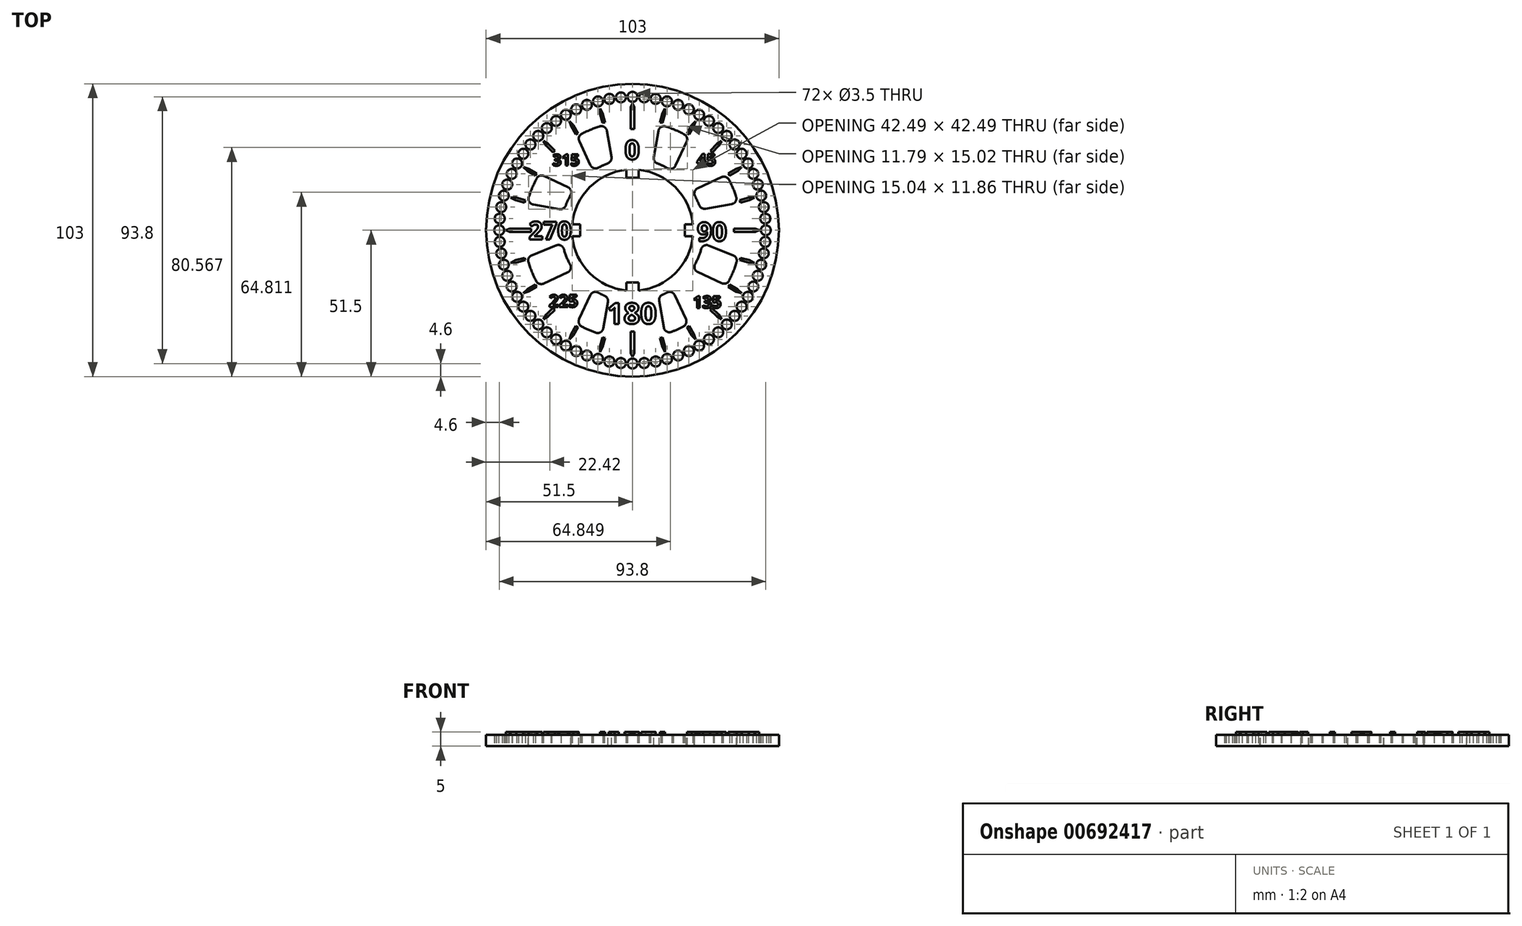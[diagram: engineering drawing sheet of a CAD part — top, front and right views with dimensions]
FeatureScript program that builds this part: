
annotation { "Feature Type Name" : "Feature", "Feature Type Description" : "" }
export const myFeature = defineFeature(function(context is Context, id is Id, definition is map)
    precondition{}
    {
        {
            var Q0;
            Q0=qCreatedBy(makeId("Top.planeOp"),FACE);
            var sketch = newSketch(context, id + "F0", { "sketchPlane" : qUnion([Q0])});
            skArc(sketch, "E0", {"start": v(-2.45, 20.86) * mm, "mid": v(-14.85, 14.85) * mm, "end": v(-20.86, 2.45) * mm});
            skLineSegment(sketch, "E1", {"start": v(0, 35.66) * mm, "end": v(0, -32.33) * mm, "construction": true});
            skLineSegment(sketch, "E2", {"start": v(-36.79, 0) * mm, "end": v(39.43, 0) * mm, "construction": true});
            skCircle(sketch, "E3", {"center": v(0, 0) * mm, "radius": 21.35 * mm});
            skLineSegment(sketch, "E4", {"start": v(0, 18.06) * mm, "end": v(-2.45, 18.06) * mm});
            skLineSegment(sketch, "E5", {"start": v(-2.45, 18.06) * mm, "end": v(-2.45, 20.86) * mm});
            skLineSegment(sketch, "E6.MirrorCS", {"start": v(0, 18.06) * mm, "end": v(2.45, 18.06) * mm});
            skLineSegment(sketch, "E7.MirrorCS", {"start": v(2.45, 18.06) * mm, "end": v(2.45, 20.86) * mm});
            skLineSegment(sketch, "E8.1.0", {"start": v(-18.06, -2.45) * mm, "end": v(-20.86, -2.45) * mm});
            skLineSegment(sketch, "E8.1.1", {"start": v(-18.06, 0) * mm, "end": v(-18.06, -2.45) * mm});
            skLineSegment(sketch, "E8.1.2", {"start": v(-18.06, 0) * mm, "end": v(-18.06, 2.45) * mm});
            skLineSegment(sketch, "E8.1.3", {"start": v(-18.06, 2.45) * mm, "end": v(-20.86, 2.45) * mm});
            skLineSegment(sketch, "E8.2.0", {"start": v(2.45, -18.06) * mm, "end": v(2.45, -20.86) * mm});
            skLineSegment(sketch, "E8.2.1", {"start": v(0, -18.06) * mm, "end": v(2.45, -18.06) * mm});
            skLineSegment(sketch, "E8.2.2", {"start": v(0, -18.06) * mm, "end": v(-2.45, -18.06) * mm});
            skLineSegment(sketch, "E8.2.3", {"start": v(-2.45, -18.06) * mm, "end": v(-2.45, -20.86) * mm});
            skLineSegment(sketch, "E8.3.0", {"start": v(18.06, 2.45) * mm, "end": v(20.86, 2.45) * mm});
            skLineSegment(sketch, "E8.3.1", {"start": v(18.06, 0) * mm, "end": v(18.06, 2.45) * mm});
            skLineSegment(sketch, "E8.3.2", {"start": v(18.06, 0) * mm, "end": v(18.06, -2.45) * mm});
            skLineSegment(sketch, "E8.3.3", {"start": v(18.06, -2.45) * mm, "end": v(20.86, -2.45) * mm});
            skArc(sketch, "E9.trimOffspring", {"start": v(20.86, 2.45) * mm, "mid": v(14.85, 14.85) * mm, "end": v(2.45, 20.86) * mm});
            skArc(sketch, "E10.trimOffspring", {"start": v(2.45, -20.86) * mm, "mid": v(14.85, -14.85) * mm, "end": v(20.86, -2.45) * mm});
            skArc(sketch, "E11.trimOffspring", {"start": v(-20.86, -2.45) * mm, "mid": v(-14.85, -14.85) * mm, "end": v(-2.45, -20.86) * mm});
            skCircle(sketch, "E12", {"center": v(0, 0) * mm, "radius": 24.63 * mm});
            skLineSegment(sketch, "E13", {"start": v(-1.6, 24.58) * mm, "end": v(-1.6, 48.9) * mm});
            skLineSegment(sketch, "E14", {"start": v(-1.6, 48.9) * mm, "end": v(1.67, 48.9) * mm});
            skLineSegment(sketch, "E15", {"start": v(1.67, 48.9) * mm, "end": v(1.67, 24.58) * mm});
            skCircle(sketch, "E16", {"center": v(0, 0) * mm, "radius": 21 * mm, "construction": true});
            skPoint(sketch, "E17", {"position": v(0, 21) * mm});
            skLineSegment(sketch, "E18", {"start": v(-7.13, 21) * mm, "end": v(7.07, 21) * mm, "construction": true});
            skPoint(sketch, "E19", {"position": v(0, 46.9) * mm});
            skLineSegment(sketch, "E20", {"start": v(-18.06, 46.9) * mm, "end": v(18.78, 46.9) * mm, "construction": true});
            skCircle(sketch, "E21", {"center": v(0, 46.9) * mm, "radius": 1.75 * mm});
            skLineSegment(sketch, "E22", {"start": v(-2.1, 21.25) * mm, "end": v(-2.1, 18.4) * mm});
            skLineSegment(sketch, "E23", {"start": v(-2.1, 18.4) * mm, "end": v(2.1, 18.4) * mm});
            skLineSegment(sketch, "E24", {"start": v(2.1, 18.4) * mm, "end": v(2.1, 21.25) * mm});
            skLineSegment(sketch, "E25.1.0", {"start": v(-21.25, -2.1) * mm, "end": v(-18.4, -2.1) * mm});
            skLineSegment(sketch, "E25.1.1", {"start": v(-18.4, -2.1) * mm, "end": v(-18.4, 2.1) * mm});
            skLineSegment(sketch, "E25.1.2", {"start": v(-18.4, 2.1) * mm, "end": v(-21.25, 2.1) * mm});
            skLineSegment(sketch, "E25.2.0", {"start": v(2.1, -21.25) * mm, "end": v(2.1, -18.4) * mm});
            skLineSegment(sketch, "E25.2.1", {"start": v(2.1, -18.4) * mm, "end": v(-2.1, -18.4) * mm});
            skLineSegment(sketch, "E25.2.2", {"start": v(-2.1, -18.4) * mm, "end": v(-2.1, -21.25) * mm});
            skLineSegment(sketch, "E25.3.0", {"start": v(21.25, 2.1) * mm, "end": v(18.4, 2.1) * mm});
            skLineSegment(sketch, "E25.3.1", {"start": v(18.4, 2.1) * mm, "end": v(18.4, -2.1) * mm});
            skLineSegment(sketch, "E25.3.2", {"start": v(18.4, -2.1) * mm, "end": v(21.25, -2.1) * mm});
            skCircle(sketch, "E26", {"center": v(0, 46.9) * mm, "radius": 4.35 * mm});
            skCircle(sketch, "E27", {"center": v(0, 0) * mm, "radius": 51.5 * mm});
            skCircle(sketch, "E28.1.0", {"center": v(-4.09, 46.72) * mm, "radius": 1.75 * mm});
            skCircle(sketch, "E28.2.0", {"center": v(-8.14, 46.19) * mm, "radius": 1.75 * mm});
            skCircle(sketch, "E28.3.0", {"center": v(-12.14, 45.3) * mm, "radius": 1.75 * mm});
            skCircle(sketch, "E28.4.0", {"center": v(-16.04, 44.07) * mm, "radius": 1.75 * mm});
            skCircle(sketch, "E28.5.0", {"center": v(-19.82, 42.5) * mm, "radius": 1.75 * mm});
            skCircle(sketch, "E28.6.0", {"center": v(-23.45, 40.62) * mm, "radius": 1.75 * mm});
            skCircle(sketch, "E28.7.0", {"center": v(-26.9, 38.42) * mm, "radius": 1.75 * mm});
            skCircle(sketch, "E28.8.0", {"center": v(-30.15, 35.93) * mm, "radius": 1.75 * mm});
            skCircle(sketch, "E28.9.0", {"center": v(-33.16, 33.16) * mm, "radius": 1.75 * mm});
            skCircle(sketch, "E28.10.0", {"center": v(-35.93, 30.15) * mm, "radius": 1.75 * mm});
            skCircle(sketch, "E28.11.0", {"center": v(-38.42, 26.9) * mm, "radius": 1.75 * mm});
            skCircle(sketch, "E28.12.0", {"center": v(-40.62, 23.45) * mm, "radius": 1.75 * mm});
            skCircle(sketch, "E28.13.0", {"center": v(-42.5, 19.82) * mm, "radius": 1.75 * mm});
            skCircle(sketch, "E28.14.0", {"center": v(-44.07, 16.04) * mm, "radius": 1.75 * mm});
            skCircle(sketch, "E28.15.0", {"center": v(-45.3, 12.14) * mm, "radius": 1.75 * mm});
            skCircle(sketch, "E28.16.0", {"center": v(-46.19, 8.14) * mm, "radius": 1.75 * mm});
            skCircle(sketch, "E28.17.0", {"center": v(-46.72, 4.09) * mm, "radius": 1.75 * mm});
            skCircle(sketch, "E28.18.0", {"center": v(-46.9, 0) * mm, "radius": 1.75 * mm});
            skCircle(sketch, "E28.19.0", {"center": v(-46.72, -4.09) * mm, "radius": 1.75 * mm});
            skCircle(sketch, "E28.20.0", {"center": v(-46.19, -8.14) * mm, "radius": 1.75 * mm});
            skCircle(sketch, "E28.21.0", {"center": v(-45.3, -12.14) * mm, "radius": 1.75 * mm});
            skCircle(sketch, "E28.22.0", {"center": v(-44.07, -16.04) * mm, "radius": 1.75 * mm});
            skCircle(sketch, "E28.23.0", {"center": v(-42.5, -19.82) * mm, "radius": 1.75 * mm});
            skCircle(sketch, "E28.24.0", {"center": v(-40.62, -23.45) * mm, "radius": 1.75 * mm});
            skCircle(sketch, "E28.25.0", {"center": v(-38.42, -26.9) * mm, "radius": 1.75 * mm});
            skCircle(sketch, "E28.26.0", {"center": v(-35.93, -30.15) * mm, "radius": 1.75 * mm});
            skCircle(sketch, "E28.27.0", {"center": v(-33.16, -33.16) * mm, "radius": 1.75 * mm});
            skCircle(sketch, "E28.28.0", {"center": v(-30.15, -35.93) * mm, "radius": 1.75 * mm});
            skCircle(sketch, "E28.29.0", {"center": v(-26.9, -38.42) * mm, "radius": 1.75 * mm});
            skCircle(sketch, "E28.30.0", {"center": v(-23.45, -40.62) * mm, "radius": 1.75 * mm});
            skCircle(sketch, "E28.31.0", {"center": v(-19.82, -42.5) * mm, "radius": 1.75 * mm});
            skCircle(sketch, "E28.32.0", {"center": v(-16.04, -44.07) * mm, "radius": 1.75 * mm});
            skCircle(sketch, "E28.33.0", {"center": v(-12.14, -45.3) * mm, "radius": 1.75 * mm});
            skCircle(sketch, "E28.34.0", {"center": v(-8.14, -46.19) * mm, "radius": 1.75 * mm});
            skCircle(sketch, "E28.35.0", {"center": v(-4.09, -46.72) * mm, "radius": 1.75 * mm});
            skCircle(sketch, "E28.36.0", {"center": v(0, -46.9) * mm, "radius": 1.75 * mm});
            skCircle(sketch, "E28.37.0", {"center": v(4.09, -46.72) * mm, "radius": 1.75 * mm});
            skCircle(sketch, "E28.38.0", {"center": v(8.14, -46.19) * mm, "radius": 1.75 * mm});
            skCircle(sketch, "E28.39.0", {"center": v(12.14, -45.3) * mm, "radius": 1.75 * mm});
            skCircle(sketch, "E28.40.0", {"center": v(16.04, -44.07) * mm, "radius": 1.75 * mm});
            skCircle(sketch, "E28.41.0", {"center": v(19.82, -42.5) * mm, "radius": 1.75 * mm});
            skCircle(sketch, "E28.42.0", {"center": v(23.45, -40.62) * mm, "radius": 1.75 * mm});
            skCircle(sketch, "E28.43.0", {"center": v(26.9, -38.42) * mm, "radius": 1.75 * mm});
            skCircle(sketch, "E28.44.0", {"center": v(30.15, -35.93) * mm, "radius": 1.75 * mm});
            skCircle(sketch, "E28.45.0", {"center": v(33.16, -33.16) * mm, "radius": 1.75 * mm});
            skCircle(sketch, "E28.46.0", {"center": v(35.93, -30.15) * mm, "radius": 1.75 * mm});
            skCircle(sketch, "E28.47.0", {"center": v(38.42, -26.9) * mm, "radius": 1.75 * mm});
            skCircle(sketch, "E28.48.0", {"center": v(40.62, -23.45) * mm, "radius": 1.75 * mm});
            skCircle(sketch, "E28.49.0", {"center": v(42.5, -19.82) * mm, "radius": 1.75 * mm});
            skCircle(sketch, "E28.50.0", {"center": v(44.07, -16.04) * mm, "radius": 1.75 * mm});
            skCircle(sketch, "E28.51.0", {"center": v(45.3, -12.14) * mm, "radius": 1.75 * mm});
            skCircle(sketch, "E28.52.0", {"center": v(46.19, -8.14) * mm, "radius": 1.75 * mm});
            skCircle(sketch, "E28.53.0", {"center": v(46.72, -4.09) * mm, "radius": 1.75 * mm});
            skCircle(sketch, "E28.54.0", {"center": v(46.9, 0) * mm, "radius": 1.75 * mm});
            skCircle(sketch, "E28.55.0", {"center": v(46.72, 4.09) * mm, "radius": 1.75 * mm});
            skCircle(sketch, "E28.56.0", {"center": v(46.19, 8.14) * mm, "radius": 1.75 * mm});
            skCircle(sketch, "E28.57.0", {"center": v(45.3, 12.14) * mm, "radius": 1.75 * mm});
            skCircle(sketch, "E28.58.0", {"center": v(44.07, 16.04) * mm, "radius": 1.75 * mm});
            skCircle(sketch, "E28.59.0", {"center": v(42.5, 19.82) * mm, "radius": 1.75 * mm});
            skCircle(sketch, "E28.60.0", {"center": v(40.62, 23.45) * mm, "radius": 1.75 * mm});
            skCircle(sketch, "E28.61.0", {"center": v(38.42, 26.9) * mm, "radius": 1.75 * mm});
            skCircle(sketch, "E28.62.0", {"center": v(35.93, 30.15) * mm, "radius": 1.75 * mm});
            skCircle(sketch, "E28.63.0", {"center": v(33.16, 33.16) * mm, "radius": 1.75 * mm});
            skCircle(sketch, "E28.64.0", {"center": v(30.15, 35.93) * mm, "radius": 1.75 * mm});
            skCircle(sketch, "E28.65.0", {"center": v(26.9, 38.42) * mm, "radius": 1.75 * mm});
            skCircle(sketch, "E28.66.0", {"center": v(23.45, 40.62) * mm, "radius": 1.75 * mm});
            skCircle(sketch, "E28.67.0", {"center": v(19.82, 42.5) * mm, "radius": 1.75 * mm});
            skCircle(sketch, "E28.68.0", {"center": v(16.04, 44.07) * mm, "radius": 1.75 * mm});
            skCircle(sketch, "E28.69.0", {"center": v(12.14, 45.3) * mm, "radius": 1.75 * mm});
            skCircle(sketch, "E28.70.0", {"center": v(8.14, 46.19) * mm, "radius": 1.75 * mm});
            skCircle(sketch, "E28.71.0", {"center": v(4.09, 46.72) * mm, "radius": 1.75 * mm});
            skCircle(sketch, "E29", {"center": v(0, 0) * mm, "radius": 42.33 * mm});
            skCircle(sketch, "E30", {"center": v(0, 0) * mm, "radius": 27.68 * mm});
            skSolve(sketch);
        }
        {
            var Q0;
            Q0=makeQuery(id+"F0.imprint","IMPRINT",FACE,{"disambiguationData":[TD([[makeQuery(id+"F0.imprint","IMPRINT",EDGE,{"derivedFrom":sQuery(id+"F0.wireOp",EDGE,"E27")}),1.0]])]});
            var Q1;
            {var subQ16=sQuery(id+"F0.wireOp",EDGE,"E14");Q1=makeQuery(id+"F0.imprint","IMPRINT",FACE,{"disambiguationData":[TD([[makeQuery(id+"F0.imprint","IMPRINT",EDGE,{"derivedFrom":subQ16}),1.0]])]});}
            var Q2;
            {var subQ0=sQuery(id+"F0.wireOp",EDGE,"E26");var subQ1=sQuery(id+"F0.wireOp",EDGE,"E13");var subQ2=makeQuery(id+"F0.imprint","INTERSECT",VERTEX,{"derivedFrom":[subQ1,subQ0]});Q2=makeQuery(id+"F0.imprint","IMPRINT",FACE,{"disambiguationData":[TD([[makeQuery(id+"F0.imprint","IMPRINT",EDGE,{"disambiguationData":[TD([[subQ2,-1.0]])],"derivedFrom":subQ1}),-1.0]])]});}
            var Q3;
            {var subQ0=sQuery(id+"F0.wireOp",EDGE,"E14");Q3=makeQuery(id+"F0.imprint","IMPRINT",FACE,{"disambiguationData":[TD([[makeQuery(id+"F0.imprint","IMPRINT",EDGE,{"derivedFrom":subQ0}),-1.0]])]});}
            var Q4;
            {var subQ0=sQuery(id+"F0.wireOp",EDGE,"E13");var subQ1=sQuery(id+"F0.wireOp",EDGE,"E12");var subQ2=makeQuery(id+"F0.imprint","INTERSECT",VERTEX,{"derivedFrom":[subQ1,subQ0]});Q4=makeQuery(id+"F0.imprint","IMPRINT",FACE,{"disambiguationData":[TD([[makeQuery(id+"F0.imprint","IMPRINT",EDGE,{"disambiguationData":[TD([[subQ2,1.0]])],"derivedFrom":subQ1}),-1.0]])]});}
            var Q5;
            {var subQ0=sQuery(id+"F0.wireOp",EDGE,"E3");var subQ4=makeQuery(id+"F0.imprint","INTERSECT",VERTEX,{"derivedFrom":[subQ0,sQuery(id+"F0.wireOp",EDGE,"E24")]});Q5=makeQuery(id+"F0.imprint","IMPRINT",FACE,{"disambiguationData":[TD([[makeQuery(id+"F0.imprint","IMPRINT",EDGE,{"disambiguationData":[TD([[subQ4,1.0]])],"derivedFrom":subQ0}),-1.0]])]});}
            var Q6;
            {var subQ5=sQuery(id+"F0.wireOp",EDGE,"E25.1.1");Q6=makeQuery(id+"F0.imprint","IMPRINT",FACE,{"disambiguationData":[TD([[makeQuery(id+"F0.imprint","IMPRINT",EDGE,{"derivedFrom":subQ5}),1.0]])]});}
            var Q7;
            {var subQ0=sQuery(id+"F0.wireOp",EDGE,"E22");Q7=makeQuery(id+"F0.imprint","IMPRINT",FACE,{"disambiguationData":[TD([[makeQuery(id+"F0.imprint","IMPRINT",EDGE,{"derivedFrom":subQ0}),1.0]])]});}
            var Q8;
            {var subQ5=sQuery(id+"F0.wireOp",EDGE,"E25.3.1");Q8=makeQuery(id+"F0.imprint","IMPRINT",FACE,{"disambiguationData":[TD([[makeQuery(id+"F0.imprint","IMPRINT",EDGE,{"derivedFrom":subQ5}),1.0]])]});}
            var Q9;
            {var subQ5=sQuery(id+"F0.wireOp",EDGE,"E25.2.1");Q9=makeQuery(id+"F0.imprint","IMPRINT",FACE,{"disambiguationData":[TD([[makeQuery(id+"F0.imprint","IMPRINT",EDGE,{"derivedFrom":subQ5}),1.0]])]});}
            var Q10;
            {var subQ0=sQuery(id+"F0.wireOp",EDGE,"E30");var subQ1=sQuery(id+"F0.wireOp",EDGE,"E13");var subQ2=makeQuery(id+"F0.imprint","INTERSECT",VERTEX,{"derivedFrom":[subQ1,subQ0]});Q10=makeQuery(id+"F0.imprint","IMPRINT",FACE,{"disambiguationData":[TD([[makeQuery(id+"F0.imprint","IMPRINT",EDGE,{"disambiguationData":[TD([[subQ2,-1.0]])],"derivedFrom":subQ1}),1.0]])]});}
            var Q11;
            {var subQ0=sQuery(id+"F0.wireOp",EDGE,"E13");var subQ1=sQuery(id+"F0.wireOp",EDGE,"E12");var subQ2=makeQuery(id+"F0.imprint","INTERSECT",VERTEX,{"derivedFrom":[subQ1,subQ0]});Q11=makeQuery(id+"F0.imprint","IMPRINT",FACE,{"disambiguationData":[TD([[makeQuery(id+"F0.imprint","IMPRINT",EDGE,{"disambiguationData":[TD([[subQ2,-1.0]])],"derivedFrom":subQ1}),-1.0]])]});}
            var Q12;
            {var subQ0=sQuery(id+"F0.wireOp",EDGE,"E30");var subQ1=sQuery(id+"F0.wireOp",EDGE,"E13");var subQ2=makeQuery(id+"F0.imprint","INTERSECT",VERTEX,{"derivedFrom":[subQ1,subQ0]});Q12=makeQuery(id+"F0.imprint","IMPRINT",FACE,{"disambiguationData":[TD([[makeQuery(id+"F0.imprint","IMPRINT",EDGE,{"disambiguationData":[TD([[subQ2,-1.0]])],"derivedFrom":subQ1}),-1.0]])]});}
            var Q13;
            {var subQ0=sQuery(id+"F0.wireOp",EDGE,"E29");var subQ1=sQuery(id+"F0.wireOp",EDGE,"E13");var subQ2=makeQuery(id+"F0.imprint","INTERSECT",VERTEX,{"derivedFrom":[subQ1,subQ0]});Q13=makeQuery(id+"F0.imprint","IMPRINT",FACE,{"disambiguationData":[TD([[makeQuery(id+"F0.imprint","IMPRINT",EDGE,{"disambiguationData":[TD([[subQ2,-1.0]])],"derivedFrom":subQ1}),-1.0]])]});}
            extrude(context, id + "F1", {"entities" : qUnion([Q0, Q1, Q2, Q3, Q4, Q5, Q6, Q7, Q8, Q9, Q10, Q11, Q12, Q13]), "depth" : 4 * mm});
        }
        {
            var Q0;
            Q0=makeQuery(id+"F1.opExtrude","CAP_FACE",FACE,{"disambiguationData":[OSD([sQuery(id+"F0.wireOp",EDGE,"E3"),sQuery(id+"F0.wireOp",EDGE,"E21"),sQuery(id+"F0.wireOp",EDGE,"E22"),sQuery(id+"F0.wireOp",EDGE,"E23"),sQuery(id+"F0.wireOp",EDGE,"E24"),sQuery(id+"F0.wireOp",EDGE,"E25.1.0"),sQuery(id+"F0.wireOp",EDGE,"E25.1.1"),sQuery(id+"F0.wireOp",EDGE,"E25.1.2"),sQuery(id+"F0.wireOp",EDGE,"E25.2.0"),sQuery(id+"F0.wireOp",EDGE,"E25.2.1"),sQuery(id+"F0.wireOp",EDGE,"E25.2.2"),sQuery(id+"F0.wireOp",EDGE,"E25.3.0"),sQuery(id+"F0.wireOp",EDGE,"E25.3.1"),sQuery(id+"F0.wireOp",EDGE,"E25.3.2"),sQuery(id+"F0.wireOp",EDGE,"E27"),sQuery(id+"F0.wireOp",EDGE,"E28.1.0"),sQuery(id+"F0.wireOp",EDGE,"E28.2.0"),sQuery(id+"F0.wireOp",EDGE,"E28.3.0"),sQuery(id+"F0.wireOp",EDGE,"E28.4.0"),sQuery(id+"F0.wireOp",EDGE,"E28.5.0"),sQuery(id+"F0.wireOp",EDGE,"E28.6.0"),sQuery(id+"F0.wireOp",EDGE,"E28.7.0"),sQuery(id+"F0.wireOp",EDGE,"E28.8.0"),sQuery(id+"F0.wireOp",EDGE,"E28.9.0"),sQuery(id+"F0.wireOp",EDGE,"E28.10.0"),sQuery(id+"F0.wireOp",EDGE,"E28.11.0"),sQuery(id+"F0.wireOp",EDGE,"E28.12.0"),sQuery(id+"F0.wireOp",EDGE,"E28.13.0"),sQuery(id+"F0.wireOp",EDGE,"E28.14.0"),sQuery(id+"F0.wireOp",EDGE,"E28.15.0"),sQuery(id+"F0.wireOp",EDGE,"E28.16.0"),sQuery(id+"F0.wireOp",EDGE,"E28.17.0"),sQuery(id+"F0.wireOp",EDGE,"E28.18.0"),sQuery(id+"F0.wireOp",EDGE,"E28.19.0"),sQuery(id+"F0.wireOp",EDGE,"E28.20.0"),sQuery(id+"F0.wireOp",EDGE,"E28.21.0"),sQuery(id+"F0.wireOp",EDGE,"E28.22.0"),sQuery(id+"F0.wireOp",EDGE,"E28.23.0"),sQuery(id+"F0.wireOp",EDGE,"E28.24.0"),sQuery(id+"F0.wireOp",EDGE,"E28.25.0"),sQuery(id+"F0.wireOp",EDGE,"E28.26.0"),sQuery(id+"F0.wireOp",EDGE,"E28.27.0"),sQuery(id+"F0.wireOp",EDGE,"E28.28.0"),sQuery(id+"F0.wireOp",EDGE,"E28.29.0"),sQuery(id+"F0.wireOp",EDGE,"E28.30.0"),sQuery(id+"F0.wireOp",EDGE,"E28.31.0"),sQuery(id+"F0.wireOp",EDGE,"E28.32.0"),sQuery(id+"F0.wireOp",EDGE,"E28.33.0"),sQuery(id+"F0.wireOp",EDGE,"E28.34.0"),sQuery(id+"F0.wireOp",EDGE,"E28.35.0"),sQuery(id+"F0.wireOp",EDGE,"E28.36.0"),sQuery(id+"F0.wireOp",EDGE,"E28.37.0"),sQuery(id+"F0.wireOp",EDGE,"E28.38.0"),sQuery(id+"F0.wireOp",EDGE,"E28.39.0"),sQuery(id+"F0.wireOp",EDGE,"E28.40.0"),sQuery(id+"F0.wireOp",EDGE,"E28.41.0"),sQuery(id+"F0.wireOp",EDGE,"E28.42.0"),sQuery(id+"F0.wireOp",EDGE,"E28.43.0"),sQuery(id+"F0.wireOp",EDGE,"E28.44.0"),sQuery(id+"F0.wireOp",EDGE,"E28.45.0"),sQuery(id+"F0.wireOp",EDGE,"E28.46.0"),sQuery(id+"F0.wireOp",EDGE,"E28.47.0"),sQuery(id+"F0.wireOp",EDGE,"E28.48.0"),sQuery(id+"F0.wireOp",EDGE,"E28.49.0"),sQuery(id+"F0.wireOp",EDGE,"E28.50.0"),sQuery(id+"F0.wireOp",EDGE,"E28.51.0"),sQuery(id+"F0.wireOp",EDGE,"E28.52.0"),sQuery(id+"F0.wireOp",EDGE,"E28.53.0"),sQuery(id+"F0.wireOp",EDGE,"E28.54.0"),sQuery(id+"F0.wireOp",EDGE,"E28.55.0"),sQuery(id+"F0.wireOp",EDGE,"E28.56.0"),sQuery(id+"F0.wireOp",EDGE,"E28.57.0"),sQuery(id+"F0.wireOp",EDGE,"E28.58.0"),sQuery(id+"F0.wireOp",EDGE,"E28.59.0"),sQuery(id+"F0.wireOp",EDGE,"E28.60.0"),sQuery(id+"F0.wireOp",EDGE,"E28.61.0"),sQuery(id+"F0.wireOp",EDGE,"E28.62.0"),sQuery(id+"F0.wireOp",EDGE,"E28.63.0"),sQuery(id+"F0.wireOp",EDGE,"E28.64.0"),sQuery(id+"F0.wireOp",EDGE,"E28.65.0"),sQuery(id+"F0.wireOp",EDGE,"E28.66.0"),sQuery(id+"F0.wireOp",EDGE,"E28.67.0"),sQuery(id+"F0.wireOp",EDGE,"E28.68.0"),sQuery(id+"F0.wireOp",EDGE,"E28.69.0"),sQuery(id+"F0.wireOp",EDGE,"E28.70.0"),sQuery(id+"F0.wireOp",EDGE,"E28.71.0")])],"isStart":false});
            var sketch = newSketch(context, id + "F2", { "sketchPlane" : qUnion([Q0])});
            skCircle(sketch, "E31", {"center": v(0, 0) * mm, "radius": 42.4 * mm});
            skCircle(sketch, "E32", {"center": v(0, 0) * mm, "radius": 25.92 * mm});
            skSolve(sketch);
        }
        {
            var Q0;
            Q0=makeQuery(id+"F1.opExtrude","CAP_FACE",FACE,{"disambiguationData":[OSD([sQuery(id+"F0.wireOp",EDGE,"E3"),sQuery(id+"F0.wireOp",EDGE,"E21"),sQuery(id+"F0.wireOp",EDGE,"E22"),sQuery(id+"F0.wireOp",EDGE,"E23"),sQuery(id+"F0.wireOp",EDGE,"E24"),sQuery(id+"F0.wireOp",EDGE,"E25.1.0"),sQuery(id+"F0.wireOp",EDGE,"E25.1.1"),sQuery(id+"F0.wireOp",EDGE,"E25.1.2"),sQuery(id+"F0.wireOp",EDGE,"E25.2.0"),sQuery(id+"F0.wireOp",EDGE,"E25.2.1"),sQuery(id+"F0.wireOp",EDGE,"E25.2.2"),sQuery(id+"F0.wireOp",EDGE,"E25.3.0"),sQuery(id+"F0.wireOp",EDGE,"E25.3.1"),sQuery(id+"F0.wireOp",EDGE,"E25.3.2"),sQuery(id+"F0.wireOp",EDGE,"E27"),sQuery(id+"F0.wireOp",EDGE,"E28.1.0"),sQuery(id+"F0.wireOp",EDGE,"E28.2.0"),sQuery(id+"F0.wireOp",EDGE,"E28.3.0"),sQuery(id+"F0.wireOp",EDGE,"E28.4.0"),sQuery(id+"F0.wireOp",EDGE,"E28.5.0"),sQuery(id+"F0.wireOp",EDGE,"E28.6.0"),sQuery(id+"F0.wireOp",EDGE,"E28.7.0"),sQuery(id+"F0.wireOp",EDGE,"E28.8.0"),sQuery(id+"F0.wireOp",EDGE,"E28.9.0"),sQuery(id+"F0.wireOp",EDGE,"E28.10.0"),sQuery(id+"F0.wireOp",EDGE,"E28.11.0"),sQuery(id+"F0.wireOp",EDGE,"E28.12.0"),sQuery(id+"F0.wireOp",EDGE,"E28.13.0"),sQuery(id+"F0.wireOp",EDGE,"E28.14.0"),sQuery(id+"F0.wireOp",EDGE,"E28.15.0"),sQuery(id+"F0.wireOp",EDGE,"E28.16.0"),sQuery(id+"F0.wireOp",EDGE,"E28.17.0"),sQuery(id+"F0.wireOp",EDGE,"E28.18.0"),sQuery(id+"F0.wireOp",EDGE,"E28.19.0"),sQuery(id+"F0.wireOp",EDGE,"E28.20.0"),sQuery(id+"F0.wireOp",EDGE,"E28.21.0"),sQuery(id+"F0.wireOp",EDGE,"E28.22.0"),sQuery(id+"F0.wireOp",EDGE,"E28.23.0"),sQuery(id+"F0.wireOp",EDGE,"E28.24.0"),sQuery(id+"F0.wireOp",EDGE,"E28.25.0"),sQuery(id+"F0.wireOp",EDGE,"E28.26.0"),sQuery(id+"F0.wireOp",EDGE,"E28.27.0"),sQuery(id+"F0.wireOp",EDGE,"E28.28.0"),sQuery(id+"F0.wireOp",EDGE,"E28.29.0"),sQuery(id+"F0.wireOp",EDGE,"E28.30.0"),sQuery(id+"F0.wireOp",EDGE,"E28.31.0"),sQuery(id+"F0.wireOp",EDGE,"E28.32.0"),sQuery(id+"F0.wireOp",EDGE,"E28.33.0"),sQuery(id+"F0.wireOp",EDGE,"E28.34.0"),sQuery(id+"F0.wireOp",EDGE,"E28.35.0"),sQuery(id+"F0.wireOp",EDGE,"E28.36.0"),sQuery(id+"F0.wireOp",EDGE,"E28.37.0"),sQuery(id+"F0.wireOp",EDGE,"E28.38.0"),sQuery(id+"F0.wireOp",EDGE,"E28.39.0"),sQuery(id+"F0.wireOp",EDGE,"E28.40.0"),sQuery(id+"F0.wireOp",EDGE,"E28.41.0"),sQuery(id+"F0.wireOp",EDGE,"E28.42.0"),sQuery(id+"F0.wireOp",EDGE,"E28.43.0"),sQuery(id+"F0.wireOp",EDGE,"E28.44.0"),sQuery(id+"F0.wireOp",EDGE,"E28.45.0"),sQuery(id+"F0.wireOp",EDGE,"E28.46.0"),sQuery(id+"F0.wireOp",EDGE,"E28.47.0"),sQuery(id+"F0.wireOp",EDGE,"E28.48.0"),sQuery(id+"F0.wireOp",EDGE,"E28.49.0"),sQuery(id+"F0.wireOp",EDGE,"E28.50.0"),sQuery(id+"F0.wireOp",EDGE,"E28.51.0"),sQuery(id+"F0.wireOp",EDGE,"E28.52.0"),sQuery(id+"F0.wireOp",EDGE,"E28.53.0"),sQuery(id+"F0.wireOp",EDGE,"E28.54.0"),sQuery(id+"F0.wireOp",EDGE,"E28.55.0"),sQuery(id+"F0.wireOp",EDGE,"E28.56.0"),sQuery(id+"F0.wireOp",EDGE,"E28.57.0"),sQuery(id+"F0.wireOp",EDGE,"E28.58.0"),sQuery(id+"F0.wireOp",EDGE,"E28.59.0"),sQuery(id+"F0.wireOp",EDGE,"E28.60.0"),sQuery(id+"F0.wireOp",EDGE,"E28.61.0"),sQuery(id+"F0.wireOp",EDGE,"E28.62.0"),sQuery(id+"F0.wireOp",EDGE,"E28.63.0"),sQuery(id+"F0.wireOp",EDGE,"E28.64.0"),sQuery(id+"F0.wireOp",EDGE,"E28.65.0"),sQuery(id+"F0.wireOp",EDGE,"E28.66.0"),sQuery(id+"F0.wireOp",EDGE,"E28.67.0"),sQuery(id+"F0.wireOp",EDGE,"E28.68.0"),sQuery(id+"F0.wireOp",EDGE,"E28.69.0"),sQuery(id+"F0.wireOp",EDGE,"E28.70.0"),sQuery(id+"F0.wireOp",EDGE,"E28.71.0")])],"isStart":false});
            var sketch = newSketch(context, id + "F3", { "sketchPlane" : qUnion([Q0])});
            skLineSegment(sketch, "E33", {"start": v(0, 43.22) * mm, "end": v(-0.58, 43.22) * mm});
            skLineSegment(sketch, "E34", {"start": v(-0.58, 43.22) * mm, "end": v(-0.58, 35.64) * mm});
            skLineSegment(sketch, "E35", {"start": v(-0.58, 35.64) * mm, "end": v(0, 35.64) * mm});
            skLineSegment(sketch, "E36", {"start": v(0, 44.58) * mm, "end": v(0, 29) * mm, "construction": true});
            skLineSegment(sketch, "E37.MirrorCS", {"start": v(0, 43.22) * mm, "end": v(0.58, 43.22) * mm});
            skLineSegment(sketch, "E38.MirrorCS", {"start": v(0.58, 43.22) * mm, "end": v(0.58, 35.64) * mm});
            skLineSegment(sketch, "E39.MirrorCS", {"start": v(0.58, 35.64) * mm, "end": v(0, 35.64) * mm});
            skLineSegment(sketch, "E40", {"start": v(-0.58, 43.22) * mm, "end": v(0, 44.58) * mm});
            skLineSegment(sketch, "E41", {"start": v(0.58, 43.22) * mm, "end": v(0, 44.58) * mm});
            skText(sketch, "E42", { "text": "0", "fontName": "OpenSans-Bold.ttf"});
            skLineSegment(sketch, "E43.1.0", {"start": v(-43.22, -0.58) * mm, "end": v(-44.58, 0) * mm});
            skLineSegment(sketch, "E43.1.1", {"start": v(-43.22, 0.58) * mm, "end": v(-44.58, 0) * mm});
            skLineSegment(sketch, "E43.1.2", {"start": v(-43.22, 0.58) * mm, "end": v(-35.64, 0.58) * mm});
            skLineSegment(sketch, "E43.1.3", {"start": v(-35.64, 0.58) * mm, "end": v(-35.64, 0) * mm});
            skLineSegment(sketch, "E43.1.4", {"start": v(-35.64, -0.58) * mm, "end": v(-35.64, 0) * mm});
            skLineSegment(sketch, "E43.1.5", {"start": v(-43.22, -0.58) * mm, "end": v(-35.64, -0.58) * mm});
            skLineSegment(sketch, "E43.2.0", {"start": v(0.58, -43.22) * mm, "end": v(0, -44.58) * mm});
            skLineSegment(sketch, "E43.2.1", {"start": v(-0.58, -43.22) * mm, "end": v(0, -44.58) * mm});
            skLineSegment(sketch, "E43.2.2", {"start": v(-0.58, -43.22) * mm, "end": v(-0.58, -35.64) * mm});
            skLineSegment(sketch, "E43.2.3", {"start": v(-0.58, -35.64) * mm, "end": v(0, -35.64) * mm});
            skLineSegment(sketch, "E43.2.4", {"start": v(0.58, -35.64) * mm, "end": v(0, -35.64) * mm});
            skLineSegment(sketch, "E43.2.5", {"start": v(0.58, -43.22) * mm, "end": v(0.58, -35.64) * mm});
            skLineSegment(sketch, "E43.3.0", {"start": v(43.22, 0.58) * mm, "end": v(44.58, 0) * mm});
            skLineSegment(sketch, "E43.3.1", {"start": v(43.22, -0.58) * mm, "end": v(44.58, 0) * mm});
            skLineSegment(sketch, "E43.3.2", {"start": v(43.22, -0.58) * mm, "end": v(35.64, -0.58) * mm});
            skLineSegment(sketch, "E43.3.3", {"start": v(35.64, -0.58) * mm, "end": v(35.64, 0) * mm});
            skLineSegment(sketch, "E43.3.4", {"start": v(35.64, 0.58) * mm, "end": v(35.64, 0) * mm});
            skLineSegment(sketch, "E43.3.5", {"start": v(43.22, 0.58) * mm, "end": v(35.64, 0.58) * mm});
            skPoint(sketch, "E43.center", {"position": v(0, 0) * mm});
            skText(sketch, "E44", { "text": "90", "fontName": "OpenSans-Bold.ttf"});
            skText(sketch, "E45", { "text": "180", "fontName": "OpenSans-Bold.ttf"});
            skPoint(sketch, "E46", {"position": v(0, 36.8) * mm});
            skText(sketch, "E47", { "text": "270", "fontName": "OpenSans-Bold.ttf"});
            const initialGuessF3  = {"E42": [-0.00281, 0.02492, 1, 0, 0.00675], "E44": [0.0227, -0.0038, 1, 0, 0.00662], "E45": [-0.00899, -0.03293, 1, 0, 0.00736], "E47": [-0.03652, -0.00328, 1, 0, 0.00634]};
            skSetInitialGuess(sketch, initialGuessF3);
            skSolve(sketch);
        }
        {
            var Q0;
            Q0=qSketchRegion(id+"F3",true);
            extrude(context, id + "F4", {"entities" : qUnion([Q0]), "operationType" : NewBodyOperationType.ADD, "depth" : 1 * mm});
        }
        {
            var Q0;
            {var subQ0=sQuery(id+"F0.wireOp",EDGE,"E28.27.0");var subQ1=sQuery(id+"F0.wireOp",EDGE,"E28.26.0");var subQ2=sQuery(id+"F0.wireOp",EDGE,"E28.25.0");var subQ3=sQuery(id+"F0.wireOp",EDGE,"E28.46.0");var subQ4=sQuery(id+"F0.wireOp",EDGE,"E28.24.0");var subQ5=sQuery(id+"F0.wireOp",EDGE,"E28.45.0");var subQ6=sQuery(id+"F0.wireOp",EDGE,"E28.23.0");var subQ7=sQuery(id+"F0.wireOp",EDGE,"E28.44.0");var subQ8=sQuery(id+"F0.wireOp",EDGE,"E28.22.0");var subQ9=sQuery(id+"F0.wireOp",EDGE,"E28.43.0");var subQ10=sQuery(id+"F0.wireOp",EDGE,"E28.21.0");var subQ11=sQuery(id+"F0.wireOp",EDGE,"E28.42.0");var subQ12=sQuery(id+"F0.wireOp",EDGE,"E28.20.0");var subQ13=sQuery(id+"F0.wireOp",EDGE,"E28.41.0");var subQ14=sQuery(id+"F0.wireOp",EDGE,"E28.19.0");var subQ15=sQuery(id+"F0.wireOp",EDGE,"E28.17.0");var subQ16=sQuery(id+"F0.wireOp",EDGE,"E28.16.0");var subQ17=sQuery(id+"F0.wireOp",EDGE,"E28.10.0");var subQ18=sQuery(id+"F0.wireOp",EDGE,"E28.9.0");var subQ19=sQuery(id+"F0.wireOp",EDGE,"E28.18.0");var subQ20=sQuery(id+"F0.wireOp",EDGE,"E28.40.0");var subQ21=sQuery(id+"F0.wireOp",EDGE,"E28.7.0");var subQ22=sQuery(id+"F0.wireOp",EDGE,"E28.6.0");var subQ23=sQuery(id+"F0.wireOp",EDGE,"E28.15.0");var subQ24=sQuery(id+"F0.wireOp",EDGE,"E28.37.0");var subQ25=sQuery(id+"F0.wireOp",EDGE,"E28.5.0");var subQ26=sQuery(id+"F0.wireOp",EDGE,"E28.14.0");var subQ27=sQuery(id+"F0.wireOp",EDGE,"E28.36.0");var subQ28=sQuery(id+"F0.wireOp",EDGE,"E25.1.0");var subQ29=sQuery(id+"F0.wireOp",EDGE,"E24");var subQ30=sQuery(id+"F0.wireOp",EDGE,"E23");var subQ31=sQuery(id+"F0.wireOp",EDGE,"E22");var subQ32=sQuery(id+"F0.wireOp",EDGE,"E21");var subQ33=sQuery(id+"F0.wireOp",EDGE,"E25.1.1");var subQ34=sQuery(id+"F0.wireOp",EDGE,"E28.28.0");var subQ35=sQuery(id+"F0.wireOp",EDGE,"E3");var subQ36=sQuery(id+"F0.wireOp",EDGE,"E25.3.0");var subQ37=sQuery(id+"F0.wireOp",EDGE,"E28.4.0");var subQ38=sQuery(id+"F0.wireOp",EDGE,"E28.13.0");var subQ39=sQuery(id+"F0.wireOp",EDGE,"E28.35.0");var subQ40=sQuery(id+"F0.wireOp",EDGE,"E25.2.0");var subQ41=sQuery(id+"F0.wireOp",EDGE,"E25.3.2");var subQ42=sQuery(id+"F0.wireOp",EDGE,"E25.1.2");var subQ43=sQuery(id+"F0.wireOp",EDGE,"E25.2.2");var subQ44=sQuery(id+"F0.wireOp",EDGE,"E25.2.1");var subQ45=sQuery(id+"F0.wireOp",EDGE,"E25.3.1");var subQ46=sQuery(id+"F0.wireOp",EDGE,"E28.8.0");var subQ47=sQuery(id+"F0.wireOp",EDGE,"E28.30.0");var subQ48=sQuery(id+"F0.wireOp",EDGE,"E27");var subQ49=sQuery(id+"F0.wireOp",EDGE,"E28.1.0");var subQ50=sQuery(id+"F0.wireOp",EDGE,"E28.2.0");var subQ51=sQuery(id+"F0.wireOp",EDGE,"E28.11.0");var subQ52=sQuery(id+"F0.wireOp",EDGE,"E28.33.0");var subQ53=sQuery(id+"F0.wireOp",EDGE,"E28.3.0");var subQ54=sQuery(id+"F0.wireOp",EDGE,"E28.12.0");var subQ55=sQuery(id+"F0.wireOp",EDGE,"E28.34.0");var subQ56=sQuery(id+"F0.wireOp",EDGE,"E28.29.0");var subQ57=sQuery(id+"F0.wireOp",EDGE,"E28.31.0");var subQ58=sQuery(id+"F0.wireOp",EDGE,"E28.32.0");var subQ59=sQuery(id+"F0.wireOp",EDGE,"E28.55.0");var subQ60=sQuery(id+"F0.wireOp",EDGE,"E28.58.0");var subQ61=sQuery(id+"F0.wireOp",EDGE,"E28.59.0");var subQ62=sQuery(id+"F0.wireOp",EDGE,"E28.60.0");var subQ63=sQuery(id+"F0.wireOp",EDGE,"E28.38.0");var subQ64=sQuery(id+"F0.wireOp",EDGE,"E28.61.0");var subQ65=sQuery(id+"F0.wireOp",EDGE,"E28.39.0");var subQ66=sQuery(id+"F0.wireOp",EDGE,"E28.62.0");var subQ67=sQuery(id+"F0.wireOp",EDGE,"E28.65.0");var subQ68=sQuery(id+"F0.wireOp",EDGE,"E28.66.0");var subQ69=sQuery(id+"F0.wireOp",EDGE,"E28.67.0");var subQ70=sQuery(id+"F0.wireOp",EDGE,"E28.68.0");var subQ71=sQuery(id+"F0.wireOp",EDGE,"E28.69.0");var subQ72=sQuery(id+"F0.wireOp",EDGE,"E28.47.0");var subQ73=sQuery(id+"F0.wireOp",EDGE,"E28.48.0");var subQ74=sQuery(id+"F0.wireOp",EDGE,"E28.49.0");var subQ75=sQuery(id+"F0.wireOp",EDGE,"E28.50.0");var subQ76=sQuery(id+"F0.wireOp",EDGE,"E28.51.0");var subQ77=sQuery(id+"F0.wireOp",EDGE,"E28.52.0");var subQ78=sQuery(id+"F0.wireOp",EDGE,"E28.53.0");var subQ79=sQuery(id+"F0.wireOp",EDGE,"E28.54.0");var subQ80=sQuery(id+"F0.wireOp",EDGE,"E28.56.0");var subQ81=sQuery(id+"F0.wireOp",EDGE,"E28.57.0");var subQ82=sQuery(id+"F0.wireOp",EDGE,"E28.63.0");var subQ83=sQuery(id+"F0.wireOp",EDGE,"E28.64.0");var subQ84=sQuery(id+"F0.wireOp",EDGE,"E28.70.0");var subQ85=sQuery(id+"F0.wireOp",EDGE,"E28.71.0");Q0=makeQuery(id+"F4.boolean.opBoolean","SPLIT",FACE,{"disambiguationData":[TD([makeQuery(id+"F1.opExtrude","SWEPT_FACE",FACE,{"disambiguationData":[OSD([subQ32])]})])],"derivedFrom":makeQuery(id+"F1.opExtrude","CAP_FACE",FACE,{"disambiguationData":[OSD([subQ35,subQ32,subQ31,subQ30,subQ29,subQ28,subQ33,subQ42,subQ40,subQ44,subQ43,subQ36,subQ45,subQ41,subQ48,subQ49,subQ50,subQ53,subQ37,subQ25,subQ22,subQ21,subQ46,subQ18,subQ17,subQ51,subQ54,subQ38,subQ26,subQ23,subQ16,subQ15,subQ19,subQ14,subQ12,subQ10,subQ8,subQ6,subQ4,subQ2,subQ1,subQ0,subQ34,subQ56,subQ47,subQ57,subQ58,subQ52,subQ55,subQ39,subQ27,subQ24,subQ63,subQ65,subQ20,subQ13,subQ11,subQ9,subQ7,subQ5,subQ3,subQ72,subQ73,subQ74,subQ75,subQ76,subQ77,subQ78,subQ79,subQ59,subQ80,subQ81,subQ60,subQ61,subQ62,subQ64,subQ66,subQ82,subQ83,subQ67,subQ68,subQ69,subQ70,subQ71,subQ84,subQ85])],"isStart":false})});}
            var sketch = newSketch(context, id + "F5", { "sketchPlane" : qUnion([Q0])});
            skLineSegment(sketch, "E48", {"start": v(27.37, 27.99) * mm, "end": v(29.73, 30.35) * mm});
            skLineSegment(sketch, "E49", {"start": v(29.73, 30.35) * mm, "end": v(30.36, 29.71) * mm});
            skLineSegment(sketch, "E50", {"start": v(30.36, 29.71) * mm, "end": v(28, 27.35) * mm});
            skLineSegment(sketch, "E51", {"start": v(28, 27.35) * mm, "end": v(27.37, 27.99) * mm});
            skLineSegment(sketch, "E52", {"start": v(-11.67, 0) * mm, "end": v(11.76, 0) * mm, "construction": true});
            skLineSegment(sketch, "E53", {"start": v(0, 14.21) * mm, "end": v(0, -13.47) * mm, "construction": true});
            skLineSegment(sketch, "E54", {"start": v(29.73, 30.35) * mm, "end": v(31.39, 31.39) * mm});
            skLineSegment(sketch, "E55", {"start": v(31.39, 31.39) * mm, "end": v(30.36, 29.71) * mm});
            skPoint(sketch, "E56", {"position": v(33.16, 33.16) * mm});
            skLineSegment(sketch, "E57", {"start": v(33.16, 33.16) * mm, "end": v(0, 0) * mm, "construction": true});
            skText(sketch, "E58", { "text": "45", "fontName": "OpenSans-Bold.ttf"});
            skLineSegment(sketch, "E59.1.0", {"start": v(19.2, 34.12) * mm, "end": v(20.86, 37) * mm});
            skLineSegment(sketch, "E59.1.1", {"start": v(20.86, 37) * mm, "end": v(22.2, 38.44) * mm});
            skLineSegment(sketch, "E59.1.2", {"start": v(22.2, 38.44) * mm, "end": v(21.64, 36.56) * mm});
            skLineSegment(sketch, "E59.1.3", {"start": v(21.64, 36.56) * mm, "end": v(19.97, 33.67) * mm});
            skLineSegment(sketch, "E59.1.4", {"start": v(19.97, 33.67) * mm, "end": v(19.2, 34.12) * mm});
            skLineSegment(sketch, "E59.2.0", {"start": v(9.7, 37.92) * mm, "end": v(10.57, 41.15) * mm});
            skLineSegment(sketch, "E59.2.1", {"start": v(10.57, 41.15) * mm, "end": v(11.49, 42.88) * mm});
            skLineSegment(sketch, "E59.2.2", {"start": v(11.49, 42.88) * mm, "end": v(11.44, 40.91) * mm});
            skLineSegment(sketch, "E59.2.3", {"start": v(11.44, 40.91) * mm, "end": v(10.57, 37.7) * mm});
            skLineSegment(sketch, "E59.2.4", {"start": v(10.57, 37.7) * mm, "end": v(9.7, 37.92) * mm});
            skLineSegment(sketch, "E59.3.0", {"start": v(-0.44, 39.14) * mm, "end": v(-0.44, 42.48) * mm});
            skLineSegment(sketch, "E59.3.1", {"start": v(-0.44, 42.48) * mm, "end": v(0, 44.4) * mm});
            skLineSegment(sketch, "E59.3.2", {"start": v(0, 44.4) * mm, "end": v(0.46, 42.48) * mm});
            skLineSegment(sketch, "E59.3.3", {"start": v(0.46, 42.48) * mm, "end": v(0.46, 39.14) * mm});
            skLineSegment(sketch, "E59.3.4", {"start": v(0.46, 39.14) * mm, "end": v(-0.44, 39.14) * mm});
            skLineSegment(sketch, "E59.4.0", {"start": v(-10.55, 37.7) * mm, "end": v(-11.42, 40.92) * mm});
            skLineSegment(sketch, "E59.4.1", {"start": v(-11.42, 40.92) * mm, "end": v(-11.49, 42.88) * mm});
            skLineSegment(sketch, "E59.4.2", {"start": v(-11.49, 42.88) * mm, "end": v(-10.55, 41.15) * mm});
            skLineSegment(sketch, "E59.4.3", {"start": v(-10.55, 41.15) * mm, "end": v(-9.69, 37.93) * mm});
            skLineSegment(sketch, "E59.4.4", {"start": v(-9.69, 37.93) * mm, "end": v(-10.55, 37.7) * mm});
            skLineSegment(sketch, "E59.5.0", {"start": v(-19.95, 33.68) * mm, "end": v(-21.62, 36.57) * mm});
            skLineSegment(sketch, "E59.5.1", {"start": v(-21.62, 36.57) * mm, "end": v(-22.2, 38.44) * mm});
            skLineSegment(sketch, "E59.5.2", {"start": v(-22.2, 38.44) * mm, "end": v(-20.84, 37.02) * mm});
            skLineSegment(sketch, "E59.5.3", {"start": v(-20.84, 37.02) * mm, "end": v(-19.17, 34.13) * mm});
            skLineSegment(sketch, "E59.5.4", {"start": v(-19.17, 34.13) * mm, "end": v(-19.95, 33.68) * mm});
            skLineSegment(sketch, "E59.6.0", {"start": v(-27.99, 27.37) * mm, "end": v(-30.35, 29.73) * mm});
            skLineSegment(sketch, "E59.6.1", {"start": v(-30.35, 29.73) * mm, "end": v(-31.39, 31.39) * mm});
            skLineSegment(sketch, "E59.6.2", {"start": v(-31.39, 31.39) * mm, "end": v(-29.71, 30.36) * mm});
            skLineSegment(sketch, "E59.6.3", {"start": v(-29.71, 30.36) * mm, "end": v(-27.35, 28) * mm});
            skLineSegment(sketch, "E59.6.4", {"start": v(-27.35, 28) * mm, "end": v(-27.99, 27.37) * mm});
            skLineSegment(sketch, "E59.7.0", {"start": v(-34.12, 19.2) * mm, "end": v(-37, 20.86) * mm});
            skLineSegment(sketch, "E59.7.1", {"start": v(-37, 20.86) * mm, "end": v(-38.44, 22.2) * mm});
            skLineSegment(sketch, "E59.7.2", {"start": v(-38.44, 22.2) * mm, "end": v(-36.56, 21.64) * mm});
            skLineSegment(sketch, "E59.7.3", {"start": v(-36.56, 21.64) * mm, "end": v(-33.67, 19.97) * mm});
            skLineSegment(sketch, "E59.7.4", {"start": v(-33.67, 19.97) * mm, "end": v(-34.12, 19.2) * mm});
            skLineSegment(sketch, "E59.8.0", {"start": v(-37.92, 9.7) * mm, "end": v(-41.15, 10.57) * mm});
            skLineSegment(sketch, "E59.8.1", {"start": v(-41.15, 10.57) * mm, "end": v(-42.88, 11.49) * mm});
            skLineSegment(sketch, "E59.8.2", {"start": v(-42.88, 11.49) * mm, "end": v(-40.91, 11.44) * mm});
            skLineSegment(sketch, "E59.8.3", {"start": v(-40.91, 11.44) * mm, "end": v(-37.7, 10.57) * mm});
            skLineSegment(sketch, "E59.8.4", {"start": v(-37.7, 10.57) * mm, "end": v(-37.92, 9.7) * mm});
            skLineSegment(sketch, "E59.9.0", {"start": v(-39.14, -0.44) * mm, "end": v(-42.48, -0.44) * mm});
            skLineSegment(sketch, "E59.9.1", {"start": v(-42.48, -0.44) * mm, "end": v(-44.4, 0) * mm});
            skLineSegment(sketch, "E59.9.2", {"start": v(-44.4, 0) * mm, "end": v(-42.48, 0.46) * mm});
            skLineSegment(sketch, "E59.9.3", {"start": v(-42.48, 0.46) * mm, "end": v(-39.14, 0.46) * mm});
            skLineSegment(sketch, "E59.9.4", {"start": v(-39.14, 0.46) * mm, "end": v(-39.14, -0.44) * mm});
            skLineSegment(sketch, "E59.10.0", {"start": v(-37.7, -10.55) * mm, "end": v(-40.92, -11.42) * mm});
            skLineSegment(sketch, "E59.10.1", {"start": v(-40.92, -11.42) * mm, "end": v(-42.88, -11.49) * mm});
            skLineSegment(sketch, "E59.10.2", {"start": v(-42.88, -11.49) * mm, "end": v(-41.15, -10.55) * mm});
            skLineSegment(sketch, "E59.10.3", {"start": v(-41.15, -10.55) * mm, "end": v(-37.93, -9.69) * mm});
            skLineSegment(sketch, "E59.10.4", {"start": v(-37.93, -9.69) * mm, "end": v(-37.7, -10.55) * mm});
            skLineSegment(sketch, "E59.11.0", {"start": v(-33.68, -19.95) * mm, "end": v(-36.57, -21.62) * mm});
            skLineSegment(sketch, "E59.11.1", {"start": v(-36.57, -21.62) * mm, "end": v(-38.44, -22.2) * mm});
            skLineSegment(sketch, "E59.11.2", {"start": v(-38.44, -22.2) * mm, "end": v(-37.02, -20.84) * mm});
            skLineSegment(sketch, "E59.11.3", {"start": v(-37.02, -20.84) * mm, "end": v(-34.13, -19.17) * mm});
            skLineSegment(sketch, "E59.11.4", {"start": v(-34.13, -19.17) * mm, "end": v(-33.68, -19.95) * mm});
            skLineSegment(sketch, "E59.12.0", {"start": v(-27.37, -27.99) * mm, "end": v(-29.73, -30.35) * mm});
            skLineSegment(sketch, "E59.12.1", {"start": v(-29.73, -30.35) * mm, "end": v(-31.39, -31.39) * mm});
            skLineSegment(sketch, "E59.12.2", {"start": v(-31.39, -31.39) * mm, "end": v(-30.36, -29.71) * mm});
            skLineSegment(sketch, "E59.12.3", {"start": v(-30.36, -29.71) * mm, "end": v(-28, -27.35) * mm});
            skLineSegment(sketch, "E59.12.4", {"start": v(-28, -27.35) * mm, "end": v(-27.37, -27.99) * mm});
            skLineSegment(sketch, "E59.13.0", {"start": v(-19.2, -34.12) * mm, "end": v(-20.86, -37) * mm});
            skLineSegment(sketch, "E59.13.1", {"start": v(-20.86, -37) * mm, "end": v(-22.2, -38.44) * mm});
            skLineSegment(sketch, "E59.13.2", {"start": v(-22.2, -38.44) * mm, "end": v(-21.64, -36.56) * mm});
            skLineSegment(sketch, "E59.13.3", {"start": v(-21.64, -36.56) * mm, "end": v(-19.97, -33.67) * mm});
            skLineSegment(sketch, "E59.13.4", {"start": v(-19.97, -33.67) * mm, "end": v(-19.2, -34.12) * mm});
            skLineSegment(sketch, "E59.14.0", {"start": v(-9.7, -37.92) * mm, "end": v(-10.57, -41.15) * mm});
            skLineSegment(sketch, "E59.14.1", {"start": v(-10.57, -41.15) * mm, "end": v(-11.49, -42.88) * mm});
            skLineSegment(sketch, "E59.14.2", {"start": v(-11.49, -42.88) * mm, "end": v(-11.44, -40.91) * mm});
            skLineSegment(sketch, "E59.14.3", {"start": v(-11.44, -40.91) * mm, "end": v(-10.57, -37.7) * mm});
            skLineSegment(sketch, "E59.14.4", {"start": v(-10.57, -37.7) * mm, "end": v(-9.7, -37.92) * mm});
            skLineSegment(sketch, "E59.15.0", {"start": v(0.44, -39.14) * mm, "end": v(0.44, -42.48) * mm});
            skLineSegment(sketch, "E59.15.1", {"start": v(0.44, -42.48) * mm, "end": v(0, -44.4) * mm});
            skLineSegment(sketch, "E59.15.2", {"start": v(0, -44.4) * mm, "end": v(-0.46, -42.48) * mm});
            skLineSegment(sketch, "E59.15.3", {"start": v(-0.46, -42.48) * mm, "end": v(-0.46, -39.14) * mm});
            skLineSegment(sketch, "E59.15.4", {"start": v(-0.46, -39.14) * mm, "end": v(0.44, -39.14) * mm});
            skLineSegment(sketch, "E59.16.0", {"start": v(10.55, -37.7) * mm, "end": v(11.42, -40.92) * mm});
            skLineSegment(sketch, "E59.16.1", {"start": v(11.42, -40.92) * mm, "end": v(11.49, -42.88) * mm});
            skLineSegment(sketch, "E59.16.2", {"start": v(11.49, -42.88) * mm, "end": v(10.55, -41.15) * mm});
            skLineSegment(sketch, "E59.16.3", {"start": v(10.55, -41.15) * mm, "end": v(9.69, -37.93) * mm});
            skLineSegment(sketch, "E59.16.4", {"start": v(9.69, -37.93) * mm, "end": v(10.55, -37.7) * mm});
            skLineSegment(sketch, "E59.17.0", {"start": v(19.95, -33.68) * mm, "end": v(21.62, -36.57) * mm});
            skLineSegment(sketch, "E59.17.1", {"start": v(21.62, -36.57) * mm, "end": v(22.2, -38.44) * mm});
            skLineSegment(sketch, "E59.17.2", {"start": v(22.2, -38.44) * mm, "end": v(20.84, -37.02) * mm});
            skLineSegment(sketch, "E59.17.3", {"start": v(20.84, -37.02) * mm, "end": v(19.17, -34.13) * mm});
            skLineSegment(sketch, "E59.17.4", {"start": v(19.17, -34.13) * mm, "end": v(19.95, -33.68) * mm});
            skLineSegment(sketch, "E59.18.0", {"start": v(27.99, -27.37) * mm, "end": v(30.35, -29.73) * mm});
            skLineSegment(sketch, "E59.18.1", {"start": v(30.35, -29.73) * mm, "end": v(31.39, -31.39) * mm});
            skLineSegment(sketch, "E59.18.2", {"start": v(31.39, -31.39) * mm, "end": v(29.71, -30.36) * mm});
            skLineSegment(sketch, "E59.18.3", {"start": v(29.71, -30.36) * mm, "end": v(27.35, -28) * mm});
            skLineSegment(sketch, "E59.18.4", {"start": v(27.35, -28) * mm, "end": v(27.99, -27.37) * mm});
            skLineSegment(sketch, "E59.19.0", {"start": v(34.12, -19.2) * mm, "end": v(37, -20.86) * mm});
            skLineSegment(sketch, "E59.19.1", {"start": v(37, -20.86) * mm, "end": v(38.44, -22.2) * mm});
            skLineSegment(sketch, "E59.19.2", {"start": v(38.44, -22.2) * mm, "end": v(36.56, -21.64) * mm});
            skLineSegment(sketch, "E59.19.3", {"start": v(36.56, -21.64) * mm, "end": v(33.67, -19.97) * mm});
            skLineSegment(sketch, "E59.19.4", {"start": v(33.67, -19.97) * mm, "end": v(34.12, -19.2) * mm});
            skLineSegment(sketch, "E59.20.0", {"start": v(37.92, -9.7) * mm, "end": v(41.15, -10.57) * mm});
            skLineSegment(sketch, "E59.20.1", {"start": v(41.15, -10.57) * mm, "end": v(42.88, -11.49) * mm});
            skLineSegment(sketch, "E59.20.2", {"start": v(42.88, -11.49) * mm, "end": v(40.91, -11.44) * mm});
            skLineSegment(sketch, "E59.20.3", {"start": v(40.91, -11.44) * mm, "end": v(37.7, -10.57) * mm});
            skLineSegment(sketch, "E59.20.4", {"start": v(37.7, -10.57) * mm, "end": v(37.92, -9.7) * mm});
            skLineSegment(sketch, "E59.21.0", {"start": v(39.14, 0.44) * mm, "end": v(42.48, 0.44) * mm});
            skLineSegment(sketch, "E59.21.1", {"start": v(42.48, 0.44) * mm, "end": v(44.4, 0) * mm});
            skLineSegment(sketch, "E59.21.2", {"start": v(44.4, 0) * mm, "end": v(42.48, -0.46) * mm});
            skLineSegment(sketch, "E59.21.3", {"start": v(42.48, -0.46) * mm, "end": v(39.14, -0.46) * mm});
            skLineSegment(sketch, "E59.21.4", {"start": v(39.14, -0.46) * mm, "end": v(39.14, 0.44) * mm});
            skLineSegment(sketch, "E59.22.0", {"start": v(37.7, 10.55) * mm, "end": v(40.92, 11.42) * mm});
            skLineSegment(sketch, "E59.22.1", {"start": v(40.92, 11.42) * mm, "end": v(42.88, 11.49) * mm});
            skLineSegment(sketch, "E59.22.2", {"start": v(42.88, 11.49) * mm, "end": v(41.15, 10.55) * mm});
            skLineSegment(sketch, "E59.22.3", {"start": v(41.15, 10.55) * mm, "end": v(37.93, 9.69) * mm});
            skLineSegment(sketch, "E59.22.4", {"start": v(37.93, 9.69) * mm, "end": v(37.7, 10.55) * mm});
            skLineSegment(sketch, "E59.23.0", {"start": v(33.68, 19.95) * mm, "end": v(36.57, 21.62) * mm});
            skLineSegment(sketch, "E59.23.1", {"start": v(36.57, 21.62) * mm, "end": v(38.44, 22.2) * mm});
            skLineSegment(sketch, "E59.23.2", {"start": v(38.44, 22.2) * mm, "end": v(37.02, 20.84) * mm});
            skLineSegment(sketch, "E59.23.3", {"start": v(37.02, 20.84) * mm, "end": v(34.13, 19.17) * mm});
            skLineSegment(sketch, "E59.23.4", {"start": v(34.13, 19.17) * mm, "end": v(33.68, 19.95) * mm});
            skPoint(sketch, "E59.center", {"position": v(0, 0) * mm});
            skText(sketch, "E60", { "text": "135", "fontName": "OpenSans-Bold.ttf"});
            skText(sketch, "E61", { "text": "225", "fontName": "OpenSans-Bold.ttf"});
            skText(sketch, "E62", { "text": "315", "fontName": "OpenSans-Bold.ttf"});
            skLineSegment(sketch, "E63", {"start": v(29.48, 22.68) * mm, "end": v(-26.7, 22.68) * mm, "construction": true});
            const initialGuessF5  = {"E58": [0.02268, 0.02268, 1, 0, 0.00421], "E60": [0.02124, -0.02737, 1, 0, 0.00422], "E61": [-0.02942, -0.02703, 1, 0, 0.00431], "E62": [-0.02818, 0.02271, 1, 0, 0.004]};
            skSetInitialGuess(sketch, initialGuessF5);
            skSolve(sketch);
        }
        {
            var Q0;
            Q0=qSketchRegion(id+"F5",true);
            extrude(context, id + "F6", {"entities" : qUnion([Q0]), "operationType" : NewBodyOperationType.ADD, "depth" : 1 * mm});
        }
        {
            var Q0;
            {var subQ0=sQuery(id+"F0.wireOp",EDGE,"E28.40.0");var subQ2=sQuery(id+"F0.wireOp",EDGE,"E28.39.0");var subQ4=sQuery(id+"F0.wireOp",EDGE,"E28.38.0");var subQ6=sQuery(id+"F0.wireOp",EDGE,"E28.35.0");var subQ8=sQuery(id+"F0.wireOp",EDGE,"E28.34.0");var subQ10=sQuery(id+"F0.wireOp",EDGE,"E28.33.0");var subQ12=sQuery(id+"F0.wireOp",EDGE,"E28.25.0");var subQ14=sQuery(id+"F0.wireOp",EDGE,"E28.24.0");var subQ16=sQuery(id+"F0.wireOp",EDGE,"E28.16.0");var subQ18=sQuery(id+"F0.wireOp",EDGE,"E24");var subQ20=sQuery(id+"F0.wireOp",EDGE,"E23");var subQ22=sQuery(id+"F0.wireOp",EDGE,"E21");var subQ23=makeQuery(id+"F1.opExtrude","SWEPT_FACE",FACE,{"disambiguationData":[OSD([subQ22])]});var subQ24=sQuery(id+"F0.wireOp",EDGE,"E22");var subQ25=sQuery(id+"F0.wireOp",EDGE,"E3");var subQ26=sQuery(id+"F0.wireOp",EDGE,"E25.1.2");var subQ28=sQuery(id+"F0.wireOp",EDGE,"E25.3.0");var subQ38=sQuery(id+"F0.wireOp",EDGE,"E28.32.0");var subQ41=sQuery(id+"F0.wireOp",EDGE,"E28.31.0");var subQ44=sQuery(id+"F0.wireOp",EDGE,"E28.30.0");var subQ47=sQuery(id+"F0.wireOp",EDGE,"E28.29.0");var subQ50=sQuery(id+"F0.wireOp",EDGE,"E28.28.0");var subQ53=sQuery(id+"F0.wireOp",EDGE,"E28.27.0");var subQ56=sQuery(id+"F0.wireOp",EDGE,"E28.26.0");var subQ59=sQuery(id+"F0.wireOp",EDGE,"E28.23.0");var subQ62=sQuery(id+"F0.wireOp",EDGE,"E28.22.0");var subQ65=sQuery(id+"F0.wireOp",EDGE,"E28.21.0");var subQ68=sQuery(id+"F0.wireOp",EDGE,"E28.20.0");var subQ71=sQuery(id+"F0.wireOp",EDGE,"E28.19.0");var subQ74=sQuery(id+"F0.wireOp",EDGE,"E28.18.0");var subQ77=sQuery(id+"F0.wireOp",EDGE,"E28.17.0");var subQ81=sQuery(id+"F0.wireOp",EDGE,"E28.13.0");var subQ84=sQuery(id+"F0.wireOp",EDGE,"E28.12.0");var subQ87=sQuery(id+"F0.wireOp",EDGE,"E28.11.0");var subQ90=sQuery(id+"F0.wireOp",EDGE,"E28.71.0");var subQ93=sQuery(id+"F0.wireOp",EDGE,"E28.70.0");var subQ101=sQuery(id+"F0.wireOp",EDGE,"E28.64.0");var subQ104=sQuery(id+"F0.wireOp",EDGE,"E28.63.0");var subQ112=sQuery(id+"F0.wireOp",EDGE,"E28.57.0");var subQ115=sQuery(id+"F0.wireOp",EDGE,"E28.56.0");var subQ117=sQuery(id+"F0.wireOp",EDGE,"E28.54.0");var subQ120=sQuery(id+"F0.wireOp",EDGE,"E28.53.0");var subQ123=sQuery(id+"F0.wireOp",EDGE,"E28.52.0");var subQ126=sQuery(id+"F0.wireOp",EDGE,"E28.51.0");var subQ129=sQuery(id+"F0.wireOp",EDGE,"E28.50.0");var subQ132=sQuery(id+"F0.wireOp",EDGE,"E28.49.0");var subQ134=sQuery(id+"F0.wireOp",EDGE,"E28.48.0");var subQ136=sQuery(id+"F0.wireOp",EDGE,"E28.47.0");var subQ138=sQuery(id+"F0.wireOp",EDGE,"E28.69.0");var subQ141=sQuery(id+"F0.wireOp",EDGE,"E28.68.0");var subQ144=sQuery(id+"F0.wireOp",EDGE,"E28.67.0");var subQ147=sQuery(id+"F0.wireOp",EDGE,"E28.66.0");var subQ150=sQuery(id+"F0.wireOp",EDGE,"E28.65.0");var subQ153=sQuery(id+"F0.wireOp",EDGE,"E28.62.0");var subQ156=sQuery(id+"F0.wireOp",EDGE,"E28.61.0");var subQ159=sQuery(id+"F0.wireOp",EDGE,"E28.60.0");var subQ162=sQuery(id+"F0.wireOp",EDGE,"E28.59.0");var subQ165=sQuery(id+"F0.wireOp",EDGE,"E28.58.0");var subQ168=sQuery(id+"F0.wireOp",EDGE,"E28.55.0");var subQ173=sQuery(id+"F0.wireOp",EDGE,"E28.3.0");var subQ177=sQuery(id+"F0.wireOp",EDGE,"E28.2.0");var subQ179=sQuery(id+"F0.wireOp",EDGE,"E28.1.0");var subQ181=sQuery(id+"F0.wireOp",EDGE,"E27");var subQ185=sQuery(id+"F0.wireOp",EDGE,"E28.8.0");var subQ187=sQuery(id+"F0.wireOp",EDGE,"E25.3.2");var subQ189=sQuery(id+"F0.wireOp",EDGE,"E25.3.1");var subQ192=sQuery(id+"F0.wireOp",EDGE,"E25.2.2");var subQ195=sQuery(id+"F0.wireOp",EDGE,"E25.2.1");var subQ198=sQuery(id+"F0.wireOp",EDGE,"E25.2.0");var subQ202=sQuery(id+"F0.wireOp",EDGE,"E25.1.0");var subQ204=sQuery(id+"F0.wireOp",EDGE,"E28.9.0");var subQ210=sQuery(id+"F0.wireOp",EDGE,"E28.10.0");var subQ216=sQuery(id+"F0.wireOp",EDGE,"E28.4.0");var subQ218=sQuery(id+"F0.wireOp",EDGE,"E28.5.0");var subQ222=sQuery(id+"F0.wireOp",EDGE,"E25.1.1");var subQ229=sQuery(id+"F0.wireOp",EDGE,"E28.36.0");var subQ233=sQuery(id+"F0.wireOp",EDGE,"E28.14.0");var subQ235=sQuery(id+"F0.wireOp",EDGE,"E28.37.0");var subQ239=sQuery(id+"F0.wireOp",EDGE,"E28.15.0");var subQ241=sQuery(id+"F0.wireOp",EDGE,"E28.6.0");var subQ244=sQuery(id+"F0.wireOp",EDGE,"E28.7.0");var subQ249=sQuery(id+"F0.wireOp",EDGE,"E28.41.0");var subQ253=sQuery(id+"F0.wireOp",EDGE,"E28.42.0");var subQ256=sQuery(id+"F0.wireOp",EDGE,"E28.43.0");var subQ259=sQuery(id+"F0.wireOp",EDGE,"E28.44.0");var subQ262=sQuery(id+"F0.wireOp",EDGE,"E28.45.0");var subQ265=sQuery(id+"F0.wireOp",EDGE,"E28.46.0");Q0=makeQuery(id+"F6.boolean.opBoolean","SPLIT",FACE,{"disambiguationData":[TD([subQ23])],"derivedFrom":makeQuery(id+"F4.boolean.opBoolean","SPLIT",FACE,{"disambiguationData":[TD([subQ23])],"derivedFrom":makeQuery(id+"F1.opExtrude","CAP_FACE",FACE,{"disambiguationData":[OSD([subQ25,subQ22,subQ24,subQ20,subQ18,subQ202,subQ222,subQ26,subQ198,subQ195,subQ192,subQ28,subQ189,subQ187,subQ181,subQ179,subQ177,subQ173,subQ216,subQ218,subQ241,subQ244,subQ185,subQ204,subQ210,subQ87,subQ84,subQ81,subQ233,subQ239,subQ16,subQ77,subQ74,subQ71,subQ68,subQ65,subQ62,subQ59,subQ14,subQ12,subQ56,subQ53,subQ50,subQ47,subQ44,subQ41,subQ38,subQ10,subQ8,subQ6,subQ229,subQ235,subQ4,subQ2,subQ0,subQ249,subQ253,subQ256,subQ259,subQ262,subQ265,subQ136,subQ134,subQ132,subQ129,subQ126,subQ123,subQ120,subQ117,subQ168,subQ115,subQ112,subQ165,subQ162,subQ159,subQ156,subQ153,subQ104,subQ101,subQ150,subQ147,subQ144,subQ141,subQ138,subQ93,subQ90])],"isStart":false})})});}
            var sketch = newSketch(context, id + "F7", { "sketchPlane" : qUnion([Q0])});
            skCircle(sketch, "E64", {"center": v(0, 0) * mm, "radius": 38.32 * mm});
            skCircle(sketch, "E65", {"center": v(0, 0) * mm, "radius": 25.06 * mm});
            skLineSegment(sketch, "E66", {"start": v(-9.4, 37.14) * mm, "end": v(-7.1, 24.03) * mm});
            skLineSegment(sketch, "E67", {"start": v(7.19, 24) * mm, "end": v(9.5, 37.12) * mm});
            skLineSegment(sketch, "E68", {"start": v(23.98, 7.27) * mm, "end": v(37.1, 9.58) * mm});
            skLineSegment(sketch, "E69", {"start": v(24.65, -4.5) * mm, "end": v(37.11, -9.53) * mm});
            skLineSegment(sketch, "E70", {"start": v(-24.03, 7.11) * mm, "end": v(-37.14, 9.42) * mm});
            skLineSegment(sketch, "E71", {"start": v(-24.66, -4.46) * mm, "end": v(-37.12, -9.5) * mm});
            skLineSegment(sketch, "E72", {"start": v(-8.38, -23.61) * mm, "end": v(-10.7, -36.8) * mm});
            skLineSegment(sketch, "E73", {"start": v(9.1, -23.35) * mm, "end": v(11.42, -36.57) * mm});
            skLineSegment(sketch, "E74", {"start": v(-19.51, 32.98) * mm, "end": v(-13.87, 20.87) * mm});
            skLineSegment(sketch, "E75", {"start": v(-32.78, 19.83) * mm, "end": v(-20.66, 14.18) * mm});
            skLineSegment(sketch, "E76", {"start": v(14.18, 20.66) * mm, "end": v(19.84, 32.78) * mm});
            skLineSegment(sketch, "E77", {"start": v(20.91, 13.8) * mm, "end": v(33.01, 19.45) * mm});
            skLineSegment(sketch, "E78", {"start": v(13.93, -20.83) * mm, "end": v(19.58, -32.94) * mm});
            skLineSegment(sketch, "E79", {"start": v(20.92, -13.79) * mm, "end": v(33.02, -19.43) * mm});
            skLineSegment(sketch, "E80", {"start": v(-20.83, -13.92) * mm, "end": v(-32.94, -19.57) * mm});
            skLineSegment(sketch, "E81", {"start": v(-13.92, -20.84) * mm, "end": v(-19.57, -32.94) * mm});
            skLineSegment(sketch, "E82", {"start": v(-9.04, 0) * mm, "end": v(11.2, 0) * mm, "construction": true});
            skLineSegment(sketch, "E83", {"start": v(0, 7.83) * mm, "end": v(0, -6.14) * mm, "construction": true});
            skSolve(sketch);
        }
        {
            var Q0;
            {var subQ0=sQuery(id+"F7.wireOp",EDGE,"E66");Q0=makeQuery(id+"F7.imprint","IMPRINT",FACE,{"disambiguationData":[TD([[makeQuery(id+"F7.imprint","IMPRINT",EDGE,{"derivedFrom":subQ0}),-1.0]])]});}
            var Q1;
            {var subQ0=sQuery(id+"F7.wireOp",EDGE,"E67");Q1=makeQuery(id+"F7.imprint","IMPRINT",FACE,{"disambiguationData":[TD([[makeQuery(id+"F7.imprint","IMPRINT",EDGE,{"derivedFrom":subQ0}),-1.0]])]});}
            var Q2;
            {var subQ0=sQuery(id+"F7.wireOp",EDGE,"E68");Q2=makeQuery(id+"F7.imprint","IMPRINT",FACE,{"disambiguationData":[TD([[makeQuery(id+"F7.imprint","IMPRINT",EDGE,{"derivedFrom":subQ0}),1.0]])]});}
            var Q3;
            {var subQ0=sQuery(id+"F7.wireOp",EDGE,"E69");Q3=makeQuery(id+"F7.imprint","IMPRINT",FACE,{"disambiguationData":[TD([[makeQuery(id+"F7.imprint","IMPRINT",EDGE,{"derivedFrom":subQ0}),-1.0]])]});}
            var Q4;
            {var subQ0=sQuery(id+"F7.wireOp",EDGE,"E73");Q4=makeQuery(id+"F7.imprint","IMPRINT",FACE,{"disambiguationData":[TD([[makeQuery(id+"F7.imprint","IMPRINT",EDGE,{"derivedFrom":subQ0}),1.0]])]});}
            var Q5;
            {var subQ0=sQuery(id+"F7.wireOp",EDGE,"E72");Q5=makeQuery(id+"F7.imprint","IMPRINT",FACE,{"disambiguationData":[TD([[makeQuery(id+"F7.imprint","IMPRINT",EDGE,{"derivedFrom":subQ0}),-1.0]])]});}
            var Q6;
            {var subQ0=sQuery(id+"F7.wireOp",EDGE,"E71");Q6=makeQuery(id+"F7.imprint","IMPRINT",FACE,{"disambiguationData":[TD([[makeQuery(id+"F7.imprint","IMPRINT",EDGE,{"derivedFrom":subQ0}),1.0]])]});}
            var Q7;
            {var subQ0=sQuery(id+"F7.wireOp",EDGE,"E70");Q7=makeQuery(id+"F7.imprint","IMPRINT",FACE,{"disambiguationData":[TD([[makeQuery(id+"F7.imprint","IMPRINT",EDGE,{"derivedFrom":subQ0}),-1.0]])]});}
            extrude(context, id + "F8", {"entities" : qUnion([Q0, Q1, Q2, Q3, Q4, Q5, Q6, Q7]), "operationType" : NewBodyOperationType.REMOVE, "endBound" : BoundingType.THROUGH_ALL, "oppositeDirection" : true, "depth" : 25 * mm});
        }
        {
            var Q0;
            Q0=makeQuery(id+"F8.boolean.opBoolean","COPY",EDGE,{"derivedFrom":makeQuery(id+"F8.opExtrude","SWEPT_EDGE",EDGE,{"disambiguationData":[OSD([sQuery(id+"F7.wireOp",EDGE,"E65"),sQuery(id+"F7.wireOp",EDGE,"E74")])]})});
            var Q1;
            Q1=makeQuery(id+"F8.boolean.opBoolean","COPY",EDGE,{"derivedFrom":makeQuery(id+"F8.opExtrude","SWEPT_EDGE",EDGE,{"disambiguationData":[OSD([sQuery(id+"F7.wireOp",EDGE,"E65"),sQuery(id+"F7.wireOp",EDGE,"E66")])]})});
            var Q2;
            Q2=makeQuery(id+"F8.boolean.opBoolean","COPY",EDGE,{"derivedFrom":makeQuery(id+"F8.opExtrude","SWEPT_EDGE",EDGE,{"disambiguationData":[OSD([sQuery(id+"F7.wireOp",EDGE,"E64"),sQuery(id+"F7.wireOp",EDGE,"E74")])]})});
            var Q3;
            Q3=makeQuery(id+"F8.boolean.opBoolean","COPY",EDGE,{"derivedFrom":makeQuery(id+"F8.opExtrude","SWEPT_EDGE",EDGE,{"disambiguationData":[OSD([sQuery(id+"F7.wireOp",EDGE,"E64"),sQuery(id+"F7.wireOp",EDGE,"E66")])]})});
            var Q4;
            Q4=makeQuery(id+"F8.boolean.opBoolean","COPY",EDGE,{"derivedFrom":makeQuery(id+"F8.opExtrude","SWEPT_EDGE",EDGE,{"disambiguationData":[OSD([sQuery(id+"F7.wireOp",EDGE,"E64"),sQuery(id+"F7.wireOp",EDGE,"E67")])]})});
            var Q5;
            Q5=makeQuery(id+"F8.boolean.opBoolean","COPY",EDGE,{"derivedFrom":makeQuery(id+"F8.opExtrude","SWEPT_EDGE",EDGE,{"disambiguationData":[OSD([sQuery(id+"F7.wireOp",EDGE,"E64"),sQuery(id+"F7.wireOp",EDGE,"E76")])]})});
            var Q6;
            Q6=makeQuery(id+"F8.boolean.opBoolean","COPY",EDGE,{"derivedFrom":makeQuery(id+"F8.opExtrude","SWEPT_EDGE",EDGE,{"disambiguationData":[OSD([sQuery(id+"F7.wireOp",EDGE,"E65"),sQuery(id+"F7.wireOp",EDGE,"E67")])]})});
            var Q7;
            Q7=makeQuery(id+"F8.boolean.opBoolean","COPY",EDGE,{"derivedFrom":makeQuery(id+"F8.opExtrude","SWEPT_EDGE",EDGE,{"disambiguationData":[OSD([sQuery(id+"F7.wireOp",EDGE,"E65"),sQuery(id+"F7.wireOp",EDGE,"E76")])]})});
            var Q8;
            Q8=makeQuery(id+"F8.boolean.opBoolean","COPY",EDGE,{"derivedFrom":makeQuery(id+"F8.opExtrude","SWEPT_EDGE",EDGE,{"disambiguationData":[OSD([sQuery(id+"F7.wireOp",EDGE,"E65"),sQuery(id+"F7.wireOp",EDGE,"E77")])]})});
            var Q9;
            Q9=makeQuery(id+"F8.boolean.opBoolean","COPY",EDGE,{"derivedFrom":makeQuery(id+"F8.opExtrude","SWEPT_EDGE",EDGE,{"disambiguationData":[OSD([sQuery(id+"F7.wireOp",EDGE,"E64"),sQuery(id+"F7.wireOp",EDGE,"E68")])]})});
            var Q10;
            Q10=makeQuery(id+"F8.boolean.opBoolean","COPY",EDGE,{"derivedFrom":makeQuery(id+"F8.opExtrude","SWEPT_EDGE",EDGE,{"disambiguationData":[OSD([sQuery(id+"F7.wireOp",EDGE,"E64"),sQuery(id+"F7.wireOp",EDGE,"E77")])]})});
            var Q11;
            Q11=makeQuery(id+"F8.boolean.opBoolean","COPY",EDGE,{"derivedFrom":makeQuery(id+"F8.opExtrude","SWEPT_EDGE",EDGE,{"disambiguationData":[OSD([sQuery(id+"F7.wireOp",EDGE,"E65"),sQuery(id+"F7.wireOp",EDGE,"E68")])]})});
            var Q12;
            Q12=makeQuery(id+"F8.boolean.opBoolean","COPY",EDGE,{"derivedFrom":makeQuery(id+"F8.opExtrude","SWEPT_EDGE",EDGE,{"disambiguationData":[OSD([sQuery(id+"F7.wireOp",EDGE,"E65"),sQuery(id+"F7.wireOp",EDGE,"E69")])]})});
            var Q13;
            Q13=makeQuery(id+"F8.boolean.opBoolean","COPY",EDGE,{"derivedFrom":makeQuery(id+"F8.opExtrude","SWEPT_EDGE",EDGE,{"disambiguationData":[OSD([sQuery(id+"F7.wireOp",EDGE,"E64"),sQuery(id+"F7.wireOp",EDGE,"E69")])]})});
            var Q14;
            Q14=makeQuery(id+"F8.boolean.opBoolean","COPY",EDGE,{"derivedFrom":makeQuery(id+"F8.opExtrude","SWEPT_EDGE",EDGE,{"disambiguationData":[OSD([sQuery(id+"F7.wireOp",EDGE,"E65"),sQuery(id+"F7.wireOp",EDGE,"E79")])]})});
            var Q15;
            Q15=makeQuery(id+"F8.boolean.opBoolean","COPY",EDGE,{"derivedFrom":makeQuery(id+"F8.opExtrude","SWEPT_EDGE",EDGE,{"disambiguationData":[OSD([sQuery(id+"F7.wireOp",EDGE,"E64"),sQuery(id+"F7.wireOp",EDGE,"E79")])]})});
            var Q16;
            Q16=makeQuery(id+"F8.boolean.opBoolean","COPY",EDGE,{"derivedFrom":makeQuery(id+"F8.opExtrude","SWEPT_EDGE",EDGE,{"disambiguationData":[OSD([sQuery(id+"F7.wireOp",EDGE,"E65"),sQuery(id+"F7.wireOp",EDGE,"E78")])]})});
            var Q17;
            Q17=makeQuery(id+"F8.boolean.opBoolean","COPY",EDGE,{"derivedFrom":makeQuery(id+"F8.opExtrude","SWEPT_EDGE",EDGE,{"disambiguationData":[OSD([sQuery(id+"F7.wireOp",EDGE,"E65"),sQuery(id+"F7.wireOp",EDGE,"E73")])]})});
            var Q18;
            Q18=makeQuery(id+"F8.boolean.opBoolean","COPY",EDGE,{"derivedFrom":makeQuery(id+"F8.opExtrude","SWEPT_EDGE",EDGE,{"disambiguationData":[OSD([sQuery(id+"F7.wireOp",EDGE,"E64"),sQuery(id+"F7.wireOp",EDGE,"E78")])]})});
            var Q19;
            Q19=makeQuery(id+"F8.boolean.opBoolean","COPY",EDGE,{"derivedFrom":makeQuery(id+"F8.opExtrude","SWEPT_EDGE",EDGE,{"disambiguationData":[OSD([sQuery(id+"F7.wireOp",EDGE,"E64"),sQuery(id+"F7.wireOp",EDGE,"E73")])]})});
            var Q20;
            Q20=makeQuery(id+"F8.boolean.opBoolean","COPY",EDGE,{"derivedFrom":makeQuery(id+"F8.opExtrude","SWEPT_EDGE",EDGE,{"disambiguationData":[OSD([sQuery(id+"F7.wireOp",EDGE,"E64"),sQuery(id+"F7.wireOp",EDGE,"E81")])]})});
            var Q21;
            Q21=makeQuery(id+"F8.boolean.opBoolean","COPY",EDGE,{"derivedFrom":makeQuery(id+"F8.opExtrude","SWEPT_EDGE",EDGE,{"disambiguationData":[OSD([sQuery(id+"F7.wireOp",EDGE,"E65"),sQuery(id+"F7.wireOp",EDGE,"E81")])]})});
            var Q22;
            Q22=makeQuery(id+"F8.boolean.opBoolean","COPY",EDGE,{"derivedFrom":makeQuery(id+"F8.opExtrude","SWEPT_EDGE",EDGE,{"disambiguationData":[OSD([sQuery(id+"F7.wireOp",EDGE,"E65"),sQuery(id+"F7.wireOp",EDGE,"E72")])]})});
            var Q23;
            Q23=makeQuery(id+"F8.boolean.opBoolean","COPY",EDGE,{"derivedFrom":makeQuery(id+"F8.opExtrude","SWEPT_EDGE",EDGE,{"disambiguationData":[OSD([sQuery(id+"F7.wireOp",EDGE,"E64"),sQuery(id+"F7.wireOp",EDGE,"E72")])]})});
            var Q24;
            Q24=makeQuery(id+"F8.boolean.opBoolean","COPY",EDGE,{"derivedFrom":makeQuery(id+"F8.opExtrude","SWEPT_EDGE",EDGE,{"disambiguationData":[OSD([sQuery(id+"F7.wireOp",EDGE,"E65"),sQuery(id+"F7.wireOp",EDGE,"E71")])]})});
            var Q25;
            Q25=makeQuery(id+"F8.boolean.opBoolean","COPY",EDGE,{"derivedFrom":makeQuery(id+"F8.opExtrude","SWEPT_EDGE",EDGE,{"disambiguationData":[OSD([sQuery(id+"F7.wireOp",EDGE,"E64"),sQuery(id+"F7.wireOp",EDGE,"E80")])]})});
            var Q26;
            Q26=makeQuery(id+"F8.boolean.opBoolean","COPY",EDGE,{"derivedFrom":makeQuery(id+"F8.opExtrude","SWEPT_EDGE",EDGE,{"disambiguationData":[OSD([sQuery(id+"F7.wireOp",EDGE,"E65"),sQuery(id+"F7.wireOp",EDGE,"E80")])]})});
            var Q27;
            Q27=makeQuery(id+"F8.boolean.opBoolean","COPY",EDGE,{"derivedFrom":makeQuery(id+"F8.opExtrude","SWEPT_EDGE",EDGE,{"disambiguationData":[OSD([sQuery(id+"F7.wireOp",EDGE,"E64"),sQuery(id+"F7.wireOp",EDGE,"E71")])]})});
            var Q28;
            Q28=makeQuery(id+"F8.boolean.opBoolean","COPY",EDGE,{"derivedFrom":makeQuery(id+"F8.opExtrude","SWEPT_EDGE",EDGE,{"disambiguationData":[OSD([sQuery(id+"F7.wireOp",EDGE,"E65"),sQuery(id+"F7.wireOp",EDGE,"E70")])]})});
            var Q29;
            Q29=makeQuery(id+"F8.boolean.opBoolean","COPY",EDGE,{"derivedFrom":makeQuery(id+"F8.opExtrude","SWEPT_EDGE",EDGE,{"disambiguationData":[OSD([sQuery(id+"F7.wireOp",EDGE,"E64"),sQuery(id+"F7.wireOp",EDGE,"E70")])]})});
            var Q30;
            Q30=makeQuery(id+"F8.boolean.opBoolean","COPY",EDGE,{"derivedFrom":makeQuery(id+"F8.opExtrude","SWEPT_EDGE",EDGE,{"disambiguationData":[OSD([sQuery(id+"F7.wireOp",EDGE,"E64"),sQuery(id+"F7.wireOp",EDGE,"E75")])]})});
            var Q31;
            Q31=makeQuery(id+"F8.boolean.opBoolean","COPY",EDGE,{"derivedFrom":makeQuery(id+"F8.opExtrude","SWEPT_EDGE",EDGE,{"disambiguationData":[OSD([sQuery(id+"F7.wireOp",EDGE,"E65"),sQuery(id+"F7.wireOp",EDGE,"E75")])]})});
            fillet(context, id + "F9", {"entities" : qUnion([Q0, Q1, Q2, Q3, Q4, Q5, Q6, Q7, Q8, Q9, Q10, Q11, Q12, Q13, Q14, Q15, Q16, Q17, Q18, Q19, Q20, Q21, Q22, Q23, Q24, Q25, Q26, Q27, Q28, Q29, Q30, Q31]), "radius" : 2 * mm, "tangentPropagation" : true, "allowEdgeOverflow" : false});
        }
    });
